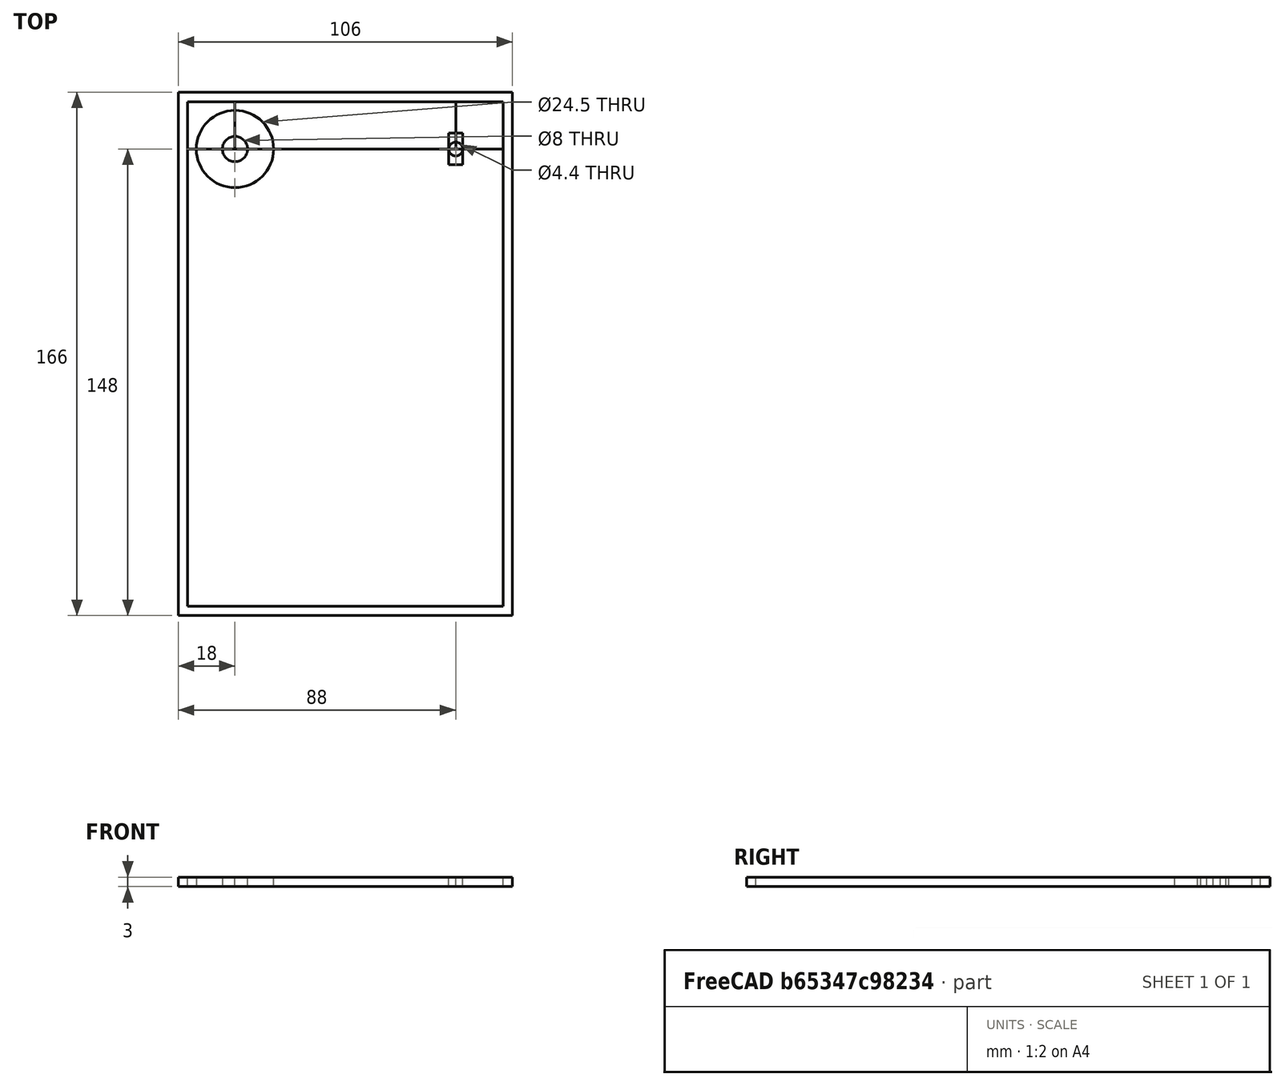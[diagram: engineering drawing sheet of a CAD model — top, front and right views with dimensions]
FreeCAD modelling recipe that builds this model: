
FCSTD DOCUMENT  (FreeCAD 0.14R2935 (Git))
Label: MysteryMachine
License: CC-BY 3.0
LicenseURL: http://creativecommons.org/licenses/by/3.0/
objects: Part::RuledSurface×2, Sketcher::SketchObject×1, Part::Extrusion×1
note: 4 computed .brp shape members not serialized (recipe doc carries the construction recipe); baked Part::Feature solids carry a one-line shape summary decoded from their .brp

FEATURE [Sketcher::SketchObject] Sketch001  label="MiddleVertical"
  sketch-geometry (24):
    g0: LineSegment StartX=-50 StartY=80 StartZ=0 EndX=50 EndY=80 EndZ=0
    g1: LineSegment StartX=50 StartY=80 StartZ=0 EndX=50 EndY=-80 EndZ=0
    g2: LineSegment StartX=50 StartY=-80 StartZ=0 EndX=-50 EndY=-80 EndZ=0
    g3: LineSegment StartX=-50 StartY=-80 StartZ=0 EndX=-50 EndY=80 EndZ=0
    g4: LineSegment StartX=-53 StartY=83 StartZ=0 EndX=53 EndY=83 EndZ=0
    g5: LineSegment StartX=53 StartY=83 StartZ=0 EndX=53 EndY=-83 EndZ=0
    g6: LineSegment StartX=53 StartY=-83 StartZ=0 EndX=-53 EndY=-83 EndZ=0
    g7: LineSegment StartX=-53 StartY=-83 StartZ=0 EndX=-53 EndY=83 EndZ=0
    g8: Circle CenterX=-35 CenterY=65 CenterZ=0 NormalX=0 NormalY=0 NormalZ=1 Radius=12.25
    g9: Circle CenterX=-35 CenterY=65 CenterZ=0 NormalX=0 NormalY=0 NormalZ=1 Radius=4
    g10: Circle CenterX=35 CenterY=65 CenterZ=0 NormalX=0 NormalY=0 NormalZ=1 Radius=2.2
    g11: LineSegment StartX=-50 StartY=80 StartZ=0 EndX=-35 EndY=80 EndZ=0
    g12: LineSegment StartX=-35 StartY=80 StartZ=0 EndX=-35 EndY=65 EndZ=0
    g13: LineSegment StartX=-35 StartY=65 StartZ=0 EndX=-50 EndY=65 EndZ=0
    g14: LineSegment StartX=-50 StartY=65 StartZ=0 EndX=-50 EndY=80 EndZ=0
    g15: LineSegment StartX=35 StartY=65 StartZ=0 EndX=50 EndY=65 EndZ=0
    g16: LineSegment StartX=50 StartY=65 StartZ=0 EndX=50 EndY=80 EndZ=0
    g17: LineSegment StartX=50 StartY=80 StartZ=0 EndX=35 EndY=80 EndZ=0
    g18: LineSegment StartX=35 StartY=80 StartZ=0 EndX=35 EndY=65 EndZ=0
    g19: LineSegment StartX=-35 StartY=65 StartZ=0 EndX=35 EndY=65 EndZ=0
    g20: LineSegment StartX=32.8 StartY=70 StartZ=0 EndX=37.2 EndY=70 EndZ=0
    g21: LineSegment StartX=37.2 StartY=70 StartZ=0 EndX=37.2 EndY=60 EndZ=0
    g22: LineSegment StartX=37.2 StartY=60 StartZ=0 EndX=32.8 EndY=60 EndZ=0
    g23: LineSegment StartX=32.8 StartY=60 StartZ=0 EndX=32.8 EndY=70 EndZ=0
  constraints (66):
    c: Coincident(g0,g1)
    c: Coincident(g1,g2)
    c: Coincident(g2,g3)
    c: Coincident(g3,g0)
    c: Horizontal(g0)
    c: Horizontal(g2)
    c: Vertical(g1)
    c: Vertical(g3)
    c: DistanceX(g0) = 100
    c: DistanceY(g3) = 160
    c: Symmetric(g0,g0,g-2)
    c: Symmetric(g0,g2,g-1)
    c: Coincident(g4,g5)
    c: Coincident(g5,g6)
    c: Coincident(g6,g7)
    c: Coincident(g7,g4)
    c: Horizontal(g4)
    c: Horizontal(g6)
    c: Vertical(g5)
    c: Vertical(g7)
    c: DistanceY(g0,g4) = 3
    c: DistanceX(g0,g4) = -3
    c: Symmetric(g4,g4,g-2)
    c: Symmetric(g4,g6,g-1)
    c: Radius(g8) = 12.25
    c: Coincident(g9,g8)
    c: Radius(g9) = 4
    c: Radius(g10) = 2.2
    c: Coincident(g11,g12)
    c: Coincident(g12,g13)
    c: Coincident(g13,g14)
    c: Coincident(g14,g11)
    c: Horizontal(g11)
    c: Horizontal(g13)
    c: Vertical(g12)
    c: Vertical(g14)
    c: Coincident(g11,g0)
    c: DistanceY(g12) = -15
    c: Equal(g12,g13)
    c: Coincident(g8,g12)
    c: Coincident(g15,g16)
    c: Coincident(g16,g17)
    c: Coincident(g17,g18)
    c: Coincident(g18,g15)
    c: Horizontal(g15)
    c: Horizontal(g17)
    c: Vertical(g16)
    c: Vertical(g18)
    c: PointOnObject(g16,g1)
    c: Symmetric(g15,g8,g-2)
    c: Coincident(g10,g15)
    c: Coincident(g19,g8)
    c: Coincident(g19,g10)
    c: Symmetric(g17,g11,g-2)
    c: Coincident(g20,g21)
    c: Coincident(g21,g22)
    c: Coincident(g22,g23)
    c: Coincident(g23,g20)
    c: Horizontal(g20)
    c: Horizontal(g22)
    c: Vertical(g21)
    c: Vertical(g23)
    c: Tangent(g23,g10)
    c: Tangent(g21,g10)
    c: DistanceY(g20,g10) = -5
    c: Symmetric(g20,g22,g19)
FEATURE [Part::RuledSurface] Ruled_Surface
  Curve1 = -> Sketch001 [Edge15]
  Curve2 = -> Sketch001 [Edge17]
  Orientation = 0
FEATURE [Part::Extrusion] Extrude
  Base = -> Sketch001
  Dir = (0,0,3)
  Solid = false
FEATURE [Part::RuledSurface] Ruled_Surface001
  Curve1 = -> Extrude [Edge47]
  Curve2 = -> Extrude [Edge42]
  Orientation = 0
